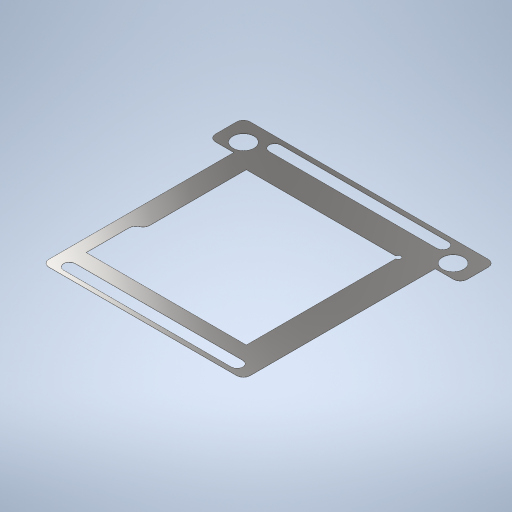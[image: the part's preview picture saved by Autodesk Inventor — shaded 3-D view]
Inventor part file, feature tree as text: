
AUTODESK INVENTOR PART (.ipt)
format: ipt  version: 2023 (Build 270158000, 158)  size: 350,720 bytes
history: native  units: in
note: dims shown in document units (in); Inventor stores cm internally (conversion verified against a paired STEP export)
features: sketch x6, extrude x5, hole x1, fillet x1
ambient origin geometry x8: Origin, YZ Plane, XZ Plane, XY Plane, X Axis, Y Axis, Z Axis, Center Point
bodies: Solid1 (feature_tree)
feature tree (13):
  extrude  "Extrusion1"  Depth=2.7in
  extrude  "Extrusion2"  TaperAngle=0.0deg  [1 undecoded]
  hole  "Hole1"  [1 undecoded]
  extrude  "Extrusion3"  Depth=0.1378in
  extrude  "Extrusion4"  Depth=2.0in
  extrude  "Extrusion5"  Depth=0.0787in
  fillet  "Fillet2"  Radius=1.0in
  sketch  "Sketch1"  dims[d0=3.0in d1=2.7in]
  sketch  "Sketch2"  dims[d2=0.002in d3=0.0in d7=0.0in d8=0.0in]
  sketch  "Sketch3"  dims[d13=2.1in d14=0.3in d16=0.4134in]
  sketch  "Sketch4"  dims[d17=0.1378in d18=0.1378in]
  sketch  "Sketch5"  dims[d19=2.0in d20=2.0in]
  sketch  "Sketch6"  dims[d21=0.125in d22=0.125in d23=1.0in d24=0.0in d27=0.0in d28=0.0in d29=0.0625in d34=1.811in d35=1.811in d36=0.5906in d37=0.0984in d38=0.0in d39=0.0in d41=0.25in d42=0.25in d43=0.25in d44=0.251in d45=0.2362in d46=0.219in d47=0.112in d48=0.5635in d49=0.315in d50=0.8108in d51=0.075in d52=0.225in d53=0.313in d54=0.0413in d55=0.0787in]
note: 2 required parameter values undecoded (feature->parameter linkage not recoverable at this tier; creation-order binding heuristic only, values carry confidence <= 0.55)
